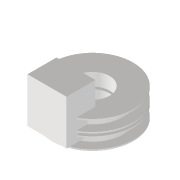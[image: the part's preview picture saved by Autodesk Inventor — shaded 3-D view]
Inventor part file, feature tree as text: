
AUTODESK INVENTOR PART (.ipt)
format: ipt  version: 2022 (Build 260153000, 153)  size: 157,184 bytes
history: native  units: mm
features: sketch x3, extrude x2, revolve x1, projected_geometry x1
ambient origin geometry x8: Origin, YZ Plane, XZ Plane, XY Plane, X Axis, Y Axis, Z Axis, Center Point
bodies: Volumenkörper1 (feature_tree)
feature tree (7):
  revolve  "Umdrehung1"
  extrude  "Extrusion1"  Depth=0.46mm
  extrude  "Extrusion2"  Depth=3.16mm
  sketch  "Skizze1"  dims[d0=13.0mm d1=0.46mm]
  sketch  "Skizze2"  dims[d2=3.0mm d3=3.16mm]
  sketch  "Skizze3"  dims[d4=0.46mm d5=20.0mm d7=4.825mm d8=10.0mm d10=10.0mm d12=90.0deg d13=12.5mm d14=14.6mm d15=7.4mm d16=7.0mm d17=0.0mm d18=0.0mm d19=12.0mm d20=0.0mm d21=0.0mm]
  projected_geometry  "Projizierte Kontur1"
